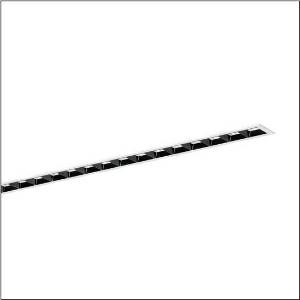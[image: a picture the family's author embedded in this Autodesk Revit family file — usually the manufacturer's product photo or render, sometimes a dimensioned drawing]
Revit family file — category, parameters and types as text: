
# Revit family: silica_r__21_51mx12dn49wb_c864
name_source: partatom
category: Lighting Fixtures
units: mm (PartAtom-declared; Revit-internal decimal feet)

## family parameters
Cut with Voids When Loaded = No
Host = Face
Light Source = No
Part Type = Normal
Room Calculation Point = No
Round Connector Dimension = Use Diameter
Shared = No

## types (1)
- --- (1 x LED, 9720 lm, 57.9 W, 4000K)
    Apparent Load = 58 VA
    CIE Flux Codes = 86 100 100 100 100
    Color Rendering = 80
    Color Temperature = 4000K
    Default Elevation = 1800 mm
    Description = Silica® 21, office luminaire, primary light control with darklight reflector, of PMMA, black, CAT 2 (L<= 3000cd/m²), light emission: direct distribution, primary light characteristic: symmetric, installation type: recessed, LED, rated luminous flux: 9.720lm, luminous efficacy: 168lm/W, light colour: 840, colour temperature: 4000K, control gear: DALI 2, with terminal, 3+2-pole, max. 2.5mm², mains connection: 220..240V, AC, 50/60Hz, rated input power: 57.9W, luminaire housing, of aluminium, traffic white (RAL 9016), length: 2.700mm, width: 79mm, height: 53mm, protection rating (complete): IP20, insulation class (complete): insulation class I (protective earthing), certification: CE, ENEC, VDE, permissible operating ambient temperature: 0..+35°C, standard: EN 50419, packaging unit: 1 piece
    Height = 0 mm  [stored 0 ft]
    Lamp = 1 x LED
    Lamp Light Flux = 9720 lm
    Lamp Power = 57.9 W
    Lamp count = 1
    Length = 2727 mm
    Luminous efficacy = 168 lm/W
    Manufacturer = Siteco
    ModVariant = No
    Model = 51MX12DN49WB
    Mounting Place = Ceiling
    Mounting Type = Recessed
    Number of Poles = 1
    OnlyDefault = Yes
    Power Factor = 1
    Product Name = Silica® 21
    Product group = office luminaire | ceiling recessed
    ProductGroupID = 400
    Protection Class = Protection class I
    Protection Degree = IP 20
    RLX_Detail_Level = 1
    RLX_Emergency_Light_Flux = 0 lm
    RLX_Emergency_Type = 0
    RLX_Emergency_Type_DB = No
    RlxData = <blob elided: 31509 chars, md5=4adf02d9>
    Socket = socket
    Standby Power = 0 W
    System Light Flux = 9720 lm
    System Power = 58 W
    Type Comments = factory setting: luminous flux: 100 % | dim-lin: 254 | 366 mA
    Type Image = l_1335880.jpg
    URL = http://relux.com
    VarID = @adj_084365
    Voltage = 0 V
    Weight = 0.00 kg
    Width = 79 mm

note: [stored X ft] marks values corroborated as IEEE doubles in the binary element streams (Revit-internal decimal feet)

## geometry (parser evidence)
native form markers: Blend x4, Sweep x11
no freeform markers — native parametric forms only
